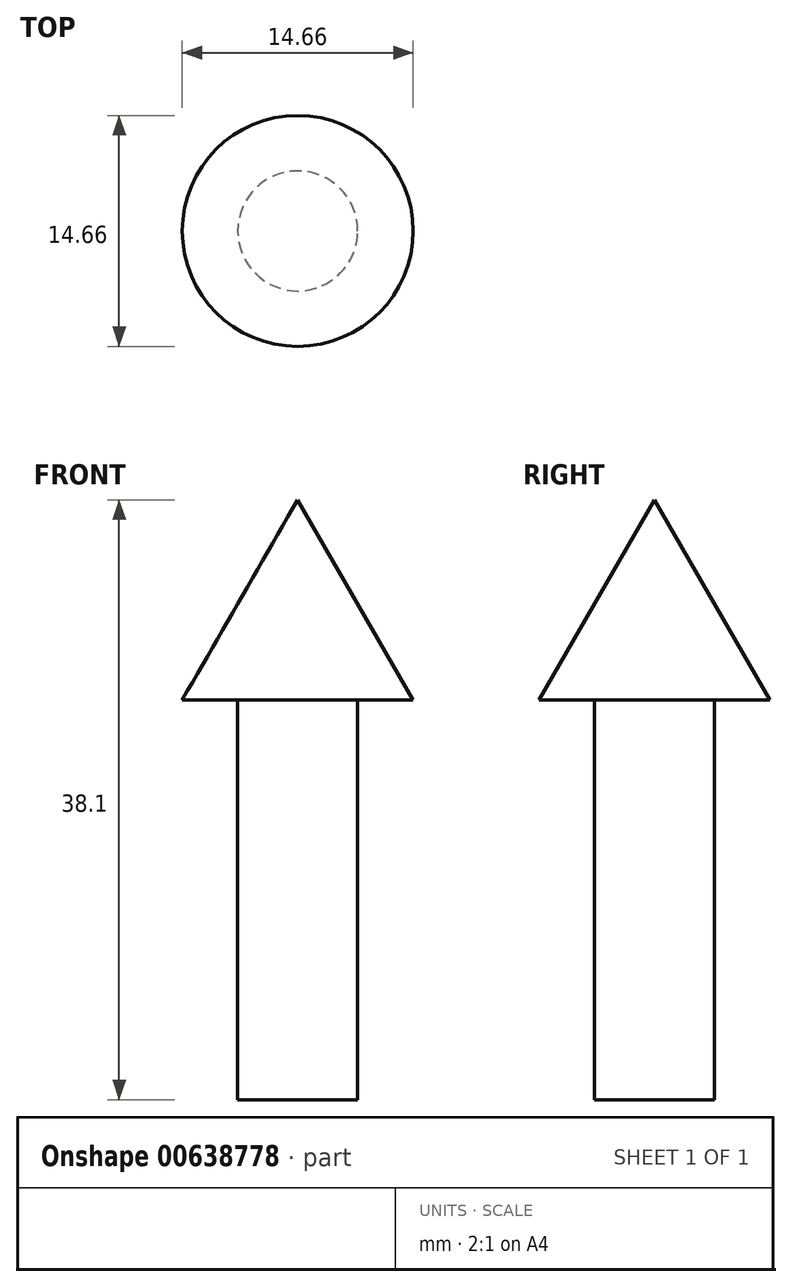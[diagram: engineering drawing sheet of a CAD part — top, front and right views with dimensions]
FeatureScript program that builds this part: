
annotation { "Feature Type Name" : "Feature", "Feature Type Description" : "" }
export const myFeature = defineFeature(function(context is Context, id is Id, definition is map)
    precondition{}
    {
        {
            var Q0;
            Q0=qCreatedBy(makeId("Front.planeOp"),FACE);
            var sketch = newSketch(context, id + "F0", { "sketchPlane" : qUnion([Q0])});
            skLineSegment(sketch, "E0", {"start": v(0, 0) * mm, "end": v(-3.8, 0) * mm});
            skLineSegment(sketch, "E1", {"start": v(-3.8, 0) * mm, "end": v(-3.8, 25.4) * mm});
            skLineSegment(sketch, "E2", {"start": v(-3.8, 25.4) * mm, "end": v(-7.33, 25.4) * mm});
            skLineSegment(sketch, "E3", {"start": v(-7.33, 25.4) * mm, "end": v(0, 38.1) * mm});
            skLineSegment(sketch, "E4", {"start": v(0, 38.1) * mm, "end": v(0, 0) * mm});
            skSolve(sketch);
        }
        {
            var Q0;
            Q0 = qSketchRegion(id + "F0", true);
            var Q1;
            Q1=sQuery(id+"F0.wireOp",EDGE,"E4");
            revolve(context, id + "F1", {"entities" : qUnion([Q0]), "axis" : qUnion([Q1]), "revolveType" : RevolveType.FULL});
        }
    });
